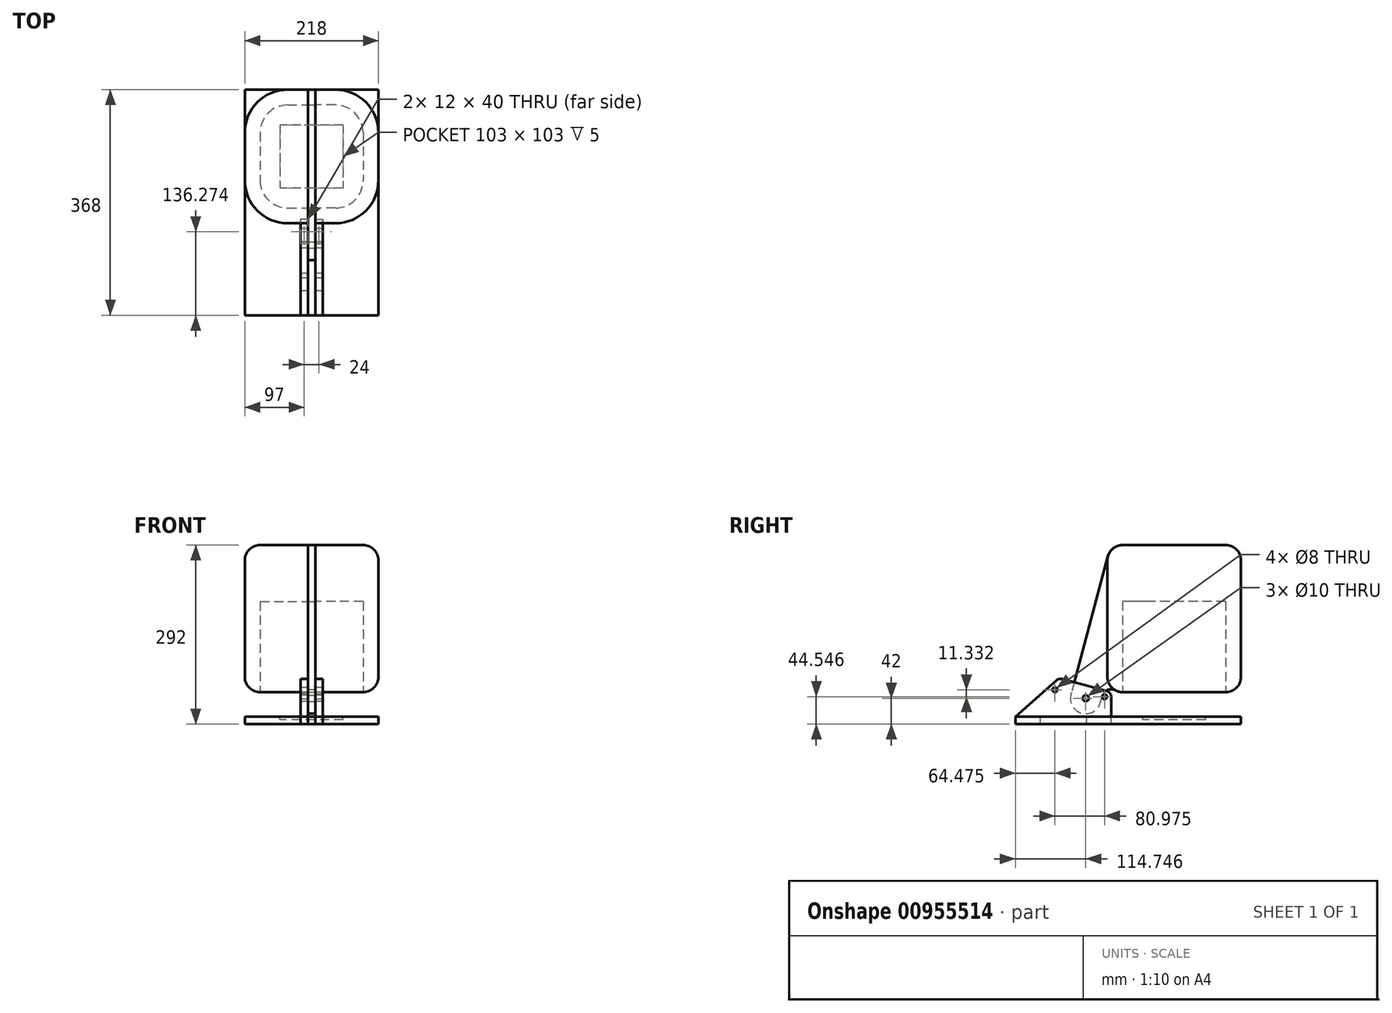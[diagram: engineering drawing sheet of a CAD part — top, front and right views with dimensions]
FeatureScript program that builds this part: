
annotation { "Feature Type Name" : "Feature", "Feature Type Description" : "" }
export const myFeature = defineFeature(function(context is Context, id is Id, definition is map)
    precondition{}
    {
        {
            assignVariable(context, id + "F0", {"name" : "mdf", "anyValue" : 12});
        }
        {
            var Q0;
            Q0=qCreatedBy(makeId("Right.planeOp"),FACE);
            var sketch = newSketch(context, id + "F1", { "sketchPlane" : qUnion([Q0])});
            skLineSegment(sketch, "E0.bottom", {"start": v(0, 0) * mm, "end": v(-35, 0) * mm});
            skLineSegment(sketch, "E0.top", {"start": v(0, 240) * mm, "end": v(-218, 240) * mm});
            skLineSegment(sketch, "E0.left", {"start": v(0, 0) * mm, "end": v(0, 240) * mm});
            skLineSegment(sketch, "E0.right", {"start": v(-218, 0) * mm, "end": v(-218, 240) * mm});
            skLineSegment(sketch, "E1.top", {"start": v(-183, 145) * mm, "end": v(-35, 145) * mm});
            skLineSegment(sketch, "E1.left", {"start": v(-183, 0) * mm, "end": v(-183, 145) * mm});
            skLineSegment(sketch, "E1.right", {"start": v(-35, 0) * mm, "end": v(-35, 145) * mm});
            skLineSegment(sketch, "E2.trimOffspring", {"start": v(-183, 0) * mm, "end": v(-218, 0) * mm});
            skLineSegment(sketch, "E3", {"start": v(-35, 0) * mm, "end": v(-183, 0) * mm});
            skSolve(sketch);
        }
        {
            var Q0;
            Q0 = qSketchRegion(id + "F1", true);
            extrude(context, id + "F2", {"entities" : qUnion([Q0]), "depth" : 103 * mm, "offsetDistance" : 25 * mm});
        }
        {
            var Q0;
            Q0=makeQuery(id+"F2.opExtrude","CAP_EDGE",EDGE,{"disambiguationData":[OSD([sQuery(id+"F1.wireOp",EDGE,"E0.left")])],"isStart":false});
            var Q1;
            Q1=makeQuery(id+"F2.opExtrude","CAP_EDGE",EDGE,{"disambiguationData":[OSD([sQuery(id+"F1.wireOp",EDGE,"E0.right")])],"isStart":false});
            fillet(context, id + "F3", {"entities" : qUnion([Q0, Q1]), "radius" : 70 * mm, "tangentPropagation" : true, "allowEdgeOverflow" : false});
        }
        {
            var Q0;
            Q0=makeQuery(id+"F2.opExtrude","SWEPT_EDGE",EDGE,{"disambiguationData":[OSD([sQuery(id+"F1.wireOp",EDGE,"E0.top"),sQuery(id+"F1.wireOp",EDGE,"E0.left")])]});
            var Q1;
            Q1=makeQuery(id+"F2.opExtrude","SWEPT_EDGE",EDGE,{"disambiguationData":[OSD([sQuery(id+"F1.wireOp",EDGE,"E0.bottom"),sQuery(id+"F1.wireOp",EDGE,"E0.left")])]});
            fillet(context, id + "F4", {"entities" : qUnion([Q0, Q1]), "radius" : 25 * mm, "tangentPropagation" : true, "allowEdgeOverflow" : false});
        }
        {
            var Q0;
            Q0=makeQuery(id+"F2.opExtrude","SWEPT_FACE",FACE,{"disambiguationData":[OSD([sQuery(id+"F1.wireOp",EDGE,"E0.bottom"),sQuery(id+"F1.wireOp",EDGE,"E2.trimOffspring"),sQuery(id+"F1.wireOp",EDGE,"E3")])]});
            var sketch = newSketch(context, id + "F5", { "sketchPlane" : qUnion([Q0])});
            skLineSegment(sketch, "E4.0", {"start": v(0, 25) * mm, "end": v(0, 193) * mm});
            skLineSegment(sketch, "E4.1", {"start": v(0, 25) * mm, "end": v(33, 25) * mm});
            skArc(sketch, "E4.2", {"start": v(33, 25) * mm, "mid": v(64.82, 38.18) * mm, "end": v(78, 70) * mm});
            skLineSegment(sketch, "E4.3", {"start": v(78, 70) * mm, "end": v(78, 148) * mm});
            skArc(sketch, "E4.4", {"start": v(78, 148) * mm, "mid": v(64.82, 179.82) * mm, "end": v(33, 193) * mm});
            skLineSegment(sketch, "E4.5", {"start": v(33, 193) * mm, "end": v(0, 193) * mm});
            skSolve(sketch);
        }
        {
            var Q0;
            Q0 = qSketchRegion(id + "F5", true);
            extrude(context, id + "F6", {"entities" : qUnion([Q0]), "operationType" : NewBodyOperationType.REMOVE, "oppositeDirection" : true, "depth" : 148 * mm, "offsetDistance" : 25 * mm});
        }
        {
            var Q0;
            Q0=makeQuery(id+"F2.opExtrude","SWEPT_BODY",BODY,{"disambiguationData":[OSD([sQuery(id+"F1.wireOp",EDGE,"E0.bottom"),sQuery(id+"F1.wireOp",EDGE,"E0.top"),sQuery(id+"F1.wireOp",EDGE,"E0.left"),sQuery(id+"F1.wireOp",EDGE,"E0.right"),sQuery(id+"F1.wireOp",EDGE,"E2.trimOffspring"),sQuery(id+"F1.wireOp",EDGE,"E3")])]});
            transform(context, id + "F7", {"entities" : qUnion([Q0]), "transformType" : TransformType.TRANSLATION_3D, "dx" : (getVariable(context, 'mdf') / 2) * mm, "dy" : 0 * mm, "dz" : 0 * mm, "makeCopy" : false});
        }
        {
            var Q0;
            Q0=makeQuery(id+"F2.opExtrude","SWEPT_BODY",BODY,{"disambiguationData":[OSD([sQuery(id+"F1.wireOp",EDGE,"E0.bottom"),sQuery(id+"F1.wireOp",EDGE,"E0.top"),sQuery(id+"F1.wireOp",EDGE,"E0.left"),sQuery(id+"F1.wireOp",EDGE,"E0.right"),sQuery(id+"F1.wireOp",EDGE,"E2.trimOffspring"),sQuery(id+"F1.wireOp",EDGE,"E3")])]});
            var Q1;
            Q1=qCreatedBy(makeId("Right.planeOp"),FACE);
            mirror(context, id + "F8", {"entities" : qUnion([Q0]), "mirrorPlane" : qUnion([Q1])});
        }
        {
            var Q0;
            Q0=makeQuery(id+"F2.opExtrude","CAP_FACE",FACE,{"disambiguationData":[OSD([sQuery(id+"F1.wireOp",EDGE,"E0.bottom"),sQuery(id+"F1.wireOp",EDGE,"E0.top"),sQuery(id+"F1.wireOp",EDGE,"E0.left"),sQuery(id+"F1.wireOp",EDGE,"E0.right"),sQuery(id+"F1.wireOp",EDGE,"E2.trimOffspring"),sQuery(id+"F1.wireOp",EDGE,"E3")])],"isStart":true});
            var sketch = newSketch(context, id + "F9", { "sketchPlane" : qUnion([Q0])});
            skLineSegment(sketch, "E5.0", {"start": v(25, 240) * mm, "end": v(193, 240) * mm});
            skArc(sketch, "E5.1", {"start": v(25, 240) * mm, "mid": v(7.32, 232.68) * mm, "end": v(0, 215) * mm});
            skLineSegment(sketch, "E5.2", {"start": v(0, 25) * mm, "end": v(0, 215) * mm});
            skArc(sketch, "E5.3", {"start": v(0, 25) * mm, "mid": v(7.32, 7.32) * mm, "end": v(25, 0) * mm});
            skLineSegment(sketch, "E5.4", {"start": v(25, 148) * mm, "end": v(25, 0) * mm});
            skLineSegment(sketch, "E5.5", {"start": v(25, 148) * mm, "end": v(193, 148) * mm});
            skLineSegment(sketch, "E5.6", {"start": v(193, 148) * mm, "end": v(193, 0) * mm});
            skArc(sketch, "E5.7", {"start": v(193, 0) * mm, "mid": v(210.68, 7.32) * mm, "end": v(218, 25) * mm});
            skLineSegment(sketch, "E5.8", {"start": v(218, 25) * mm, "end": v(218, 215) * mm});
            skArc(sketch, "E5.9", {"start": v(218, 215) * mm, "mid": v(210.68, 232.68) * mm, "end": v(193, 240) * mm});
            skLineSegment(sketch, "E6", {"start": v(217.15, 221.47) * mm, "end": v(277.4, -3.53) * mm});
            skLineSegment(sketch, "E7", {"start": v(229.1, -16.47) * mm, "end": v(218, 25) * mm});
            skArc(sketch, "E8.filletArc", {"start": v(229.1, -16.47) * mm, "mid": v(259.72, -34.15) * mm, "end": v(277.4, -3.53) * mm});
            skLineSegment(sketch, "E9.bottom", {"start": v(0, -40) * mm, "end": v(368, -40) * mm});
            skLineSegment(sketch, "E9.top", {"start": v(0, -52) * mm, "end": v(368, -52) * mm});
            skLineSegment(sketch, "E9.left", {"start": v(0, -40) * mm, "end": v(0, -52) * mm});
            skLineSegment(sketch, "E9.right", {"start": v(368, -40) * mm, "end": v(368, -52) * mm});
            skCircle(sketch, "E10", {"center": v(253.25, -10) * mm, "radius": 5 * mm});
            skLineSegment(sketch, "E11", {"start": v(211.73, -52) * mm, "end": v(211.73, 0) * mm});
            skLineSegment(sketch, "E12", {"start": v(251.73, -52) * mm, "end": v(251.73, -40) * mm});
            skLineSegment(sketch, "E13", {"start": v(251.73, -40) * mm, "end": v(328, -40) * mm});
            skLineSegment(sketch, "E14", {"start": v(328, -40) * mm, "end": v(328, -52) * mm});
            skLineSegment(sketch, "E15", {"start": v(297.18, 22.88) * mm, "end": v(368, -40) * mm});
            skLineSegment(sketch, "E16", {"start": v(211.73, 0) * mm, "end": v(297.18, 22.88) * mm});
            skCircle(sketch, "E17", {"center": v(303.53, 3.88) * mm, "radius": 4 * mm});
            skCircle(sketch, "E18", {"center": v(222.55, -7.45) * mm, "radius": 4 * mm});
            skSolve(sketch);
        }
        {
            var Q0;
            Q0=makeQuery(id+"F9.imprint","IMPRINT",FACE,{"disambiguationData":[TD([[makeQuery(id+"F9.imprint","IMPRINT",EDGE,{"derivedFrom":sQuery(id+"F9.wireOp",EDGE,"E5.0")}),-1.0]])]});
            var Q1;
            {var subQ1=sQuery(id+"F9.wireOp",EDGE,"E5.8");var subQ3=sQuery(id+"F9.wireOp",EDGE,"E6");var subQ4=makeQuery(id+"F9.imprint","INTERSECT",VERTEX,{"derivedFrom":[subQ1,subQ3]});Q1=makeQuery(id+"F9.imprint","IMPRINT",FACE,{"disambiguationData":[TD([[makeQuery(id+"F9.imprint","IMPRINT",EDGE,{"disambiguationData":[TD([[subQ4,-1.0]])],"derivedFrom":subQ3}),-1.0]])]});}
            var Q2;
            {var subQ0=sQuery(id+"F9.wireOp",EDGE,"E8.filletArc");Q2=makeQuery(id+"F9.imprint","IMPRINT",FACE,{"disambiguationData":[TD([[makeQuery(id+"F9.imprint","IMPRINT",EDGE,{"derivedFrom":subQ0}),1.0]])]});}
            extrude(context, id + "F10", {"entities" : qUnion([Q0, Q1, Q2]), "depth" : (getVariable(context, 'mdf')) * mm, "offsetDistance" : 25 * mm});
        }
        {
            var Q0;
            {var subQ0=sQuery(id+"F9.wireOp",EDGE,"E8.filletArc");Q0=makeQuery(id+"F9.imprint","IMPRINT",FACE,{"disambiguationData":[TD([[makeQuery(id+"F9.imprint","IMPRINT",EDGE,{"derivedFrom":subQ0}),1.0]])]});}
            var Q1;
            {var subQ0=sQuery(id+"F9.wireOp",EDGE,"E8.filletArc");Q1=makeQuery(id+"F9.imprint","IMPRINT",FACE,{"disambiguationData":[TD([[makeQuery(id+"F9.imprint","IMPRINT",EDGE,{"derivedFrom":subQ0}),-1.0]])]});}
            var Q2;
            {var subQ0=sQuery(id+"F9.wireOp",EDGE,"E9.right");Q2=makeQuery(id+"F9.imprint","IMPRINT",FACE,{"disambiguationData":[TD([[makeQuery(id+"F9.imprint","IMPRINT",EDGE,{"derivedFrom":subQ0}),-1.0]])]});}
            var Q3;
            {var subQ0=sQuery(id+"F9.wireOp",EDGE,"E12");Q3=makeQuery(id+"F9.imprint","IMPRINT",FACE,{"disambiguationData":[TD([[makeQuery(id+"F9.imprint","IMPRINT",EDGE,{"derivedFrom":subQ0}),1.0]])]});}
            extrude(context, id + "F11", {"entities" : qUnion([Q0, Q1, Q2, Q3]), "oppositeDirection" : true, "depth" : (getVariable(context, 'mdf')) * mm, "offsetDistance" : 25 * mm});
        }
        {
            var Q0;
            Q0=makeQuery(id+"F11.opExtrude","SWEPT_BODY",BODY,{"disambiguationData":[OSD([sQuery(id+"F9.wireOp",EDGE,"E9.top"),sQuery(id+"F9.wireOp",EDGE,"E9.right"),sQuery(id+"F9.wireOp",EDGE,"E10"),sQuery(id+"F9.wireOp",EDGE,"E11"),sQuery(id+"F9.wireOp",EDGE,"E12"),sQuery(id+"F9.wireOp",EDGE,"E13"),sQuery(id+"F9.wireOp",EDGE,"E14"),sQuery(id+"F9.wireOp",EDGE,"E15"),sQuery(id+"F9.wireOp",EDGE,"E16")])]});
            transform(context, id + "F12", {"entities" : qUnion([Q0]), "transformType" : TransformType.TRANSLATION_3D, "dx" : (-(getVariable(context, 'mdf')) * 2) * mm, "dy" : 0 * mm, "dz" : 0 * mm, "makeCopy" : true});
        }
        {
            var Q0;
            {var subQ0=sQuery(id+"F9.wireOp",EDGE,"E9.left");Q0=makeQuery(id+"F9.imprint","IMPRINT",FACE,{"disambiguationData":[TD([[makeQuery(id+"F9.imprint","IMPRINT",EDGE,{"derivedFrom":subQ0}),1.0]])]});}
            var Q1;
            {var subQ0=sQuery(id+"F9.wireOp",EDGE,"E12");Q1=makeQuery(id+"F9.imprint","IMPRINT",FACE,{"disambiguationData":[TD([[makeQuery(id+"F9.imprint","IMPRINT",EDGE,{"derivedFrom":subQ0}),1.0]])]});}
            var Q2;
            {var subQ0=sQuery(id+"F9.wireOp",EDGE,"E12");Q2=makeQuery(id+"F9.imprint","IMPRINT",FACE,{"disambiguationData":[TD([[makeQuery(id+"F9.imprint","IMPRINT",EDGE,{"derivedFrom":subQ0}),-1.0]])]});}
            var Q3;
            {var subQ0=sQuery(id+"F9.wireOp",EDGE,"E9.right");Q3=makeQuery(id+"F9.imprint","IMPRINT",FACE,{"disambiguationData":[TD([[makeQuery(id+"F9.imprint","IMPRINT",EDGE,{"derivedFrom":subQ0}),-1.0]])]});}
            var Q4;
            Q4=makeQuery(id+"F8.opPattern","COPY",FACE,{"derivedFrom":makeQuery(id+"F2.opExtrude","CAP_FACE",FACE,{"disambiguationData":[OSD([sQuery(id+"F1.wireOp",EDGE,"E0.bottom"),sQuery(id+"F1.wireOp",EDGE,"E0.top"),sQuery(id+"F1.wireOp",EDGE,"E0.left"),sQuery(id+"F1.wireOp",EDGE,"E0.right"),sQuery(id+"F1.wireOp",EDGE,"E2.trimOffspring"),sQuery(id+"F1.wireOp",EDGE,"E3")])],"isStart":false}),"instanceName":"1"});
            var Q5;
            Q5=makeQuery(id+"F2.opExtrude","CAP_FACE",FACE,{"disambiguationData":[OSD([sQuery(id+"F1.wireOp",EDGE,"E0.bottom"),sQuery(id+"F1.wireOp",EDGE,"E0.top"),sQuery(id+"F1.wireOp",EDGE,"E0.left"),sQuery(id+"F1.wireOp",EDGE,"E0.right"),sQuery(id+"F1.wireOp",EDGE,"E2.trimOffspring"),sQuery(id+"F1.wireOp",EDGE,"E3")])],"isStart":false});
            extrude(context, id + "F13", {"entities" : qUnion([Q0, Q1, Q2, Q3]), "endBound" : BoundingType.UP_TO_SURFACE, "depth" : 232 * mm, "endBoundEntityFace" : qUnion([Q4]), "offsetDistance" : 25 * mm, "hasSecondDirection" : true, "secondDirectionBound" : BoundingType.UP_TO_SURFACE, "secondDirectionOppositeDirection" : true, "secondDirectionDepth" : 25 * mm, "secondDirectionBoundEntityFace" : qUnion([Q5])});
        }
        {
            var Q0;
            Q0=makeQuery(id+"F12.opPattern","COPY",EDGE,{"derivedFrom":makeQuery(id+"F11.opExtrude","SWEPT_EDGE",EDGE,{"disambiguationData":[OSD([sQuery(id+"F9.wireOp",EDGE,"E15"),sQuery(id+"F9.wireOp",EDGE,"E16")])]}),"instanceName":"1"});
            var Q1;
            Q1=makeQuery(id+"F11.opExtrude","SWEPT_EDGE",EDGE,{"disambiguationData":[OSD([sQuery(id+"F9.wireOp",EDGE,"E15"),sQuery(id+"F9.wireOp",EDGE,"E16")])]});
            var Q2;
            Q2=makeQuery(id+"F12.opPattern","COPY",EDGE,{"derivedFrom":makeQuery(id+"F11.opExtrude","SWEPT_EDGE",EDGE,{"disambiguationData":[OSD([sQuery(id+"F9.wireOp",EDGE,"E11"),sQuery(id+"F9.wireOp",EDGE,"E16")])]}),"instanceName":"1"});
            var Q3;
            Q3=makeQuery(id+"F11.opExtrude","SWEPT_EDGE",EDGE,{"disambiguationData":[OSD([sQuery(id+"F9.wireOp",EDGE,"E11"),sQuery(id+"F9.wireOp",EDGE,"E16")])]});
            fillet(context, id + "F14", {"entities" : qUnion([Q0, Q1, Q2, Q3]), "radius" : 10 * mm, "tangentPropagation" : true, "allowEdgeOverflow" : false});
        }
        {
            var Q0;
            Q0=makeQuery(id+"F12.opPattern","COPY",BODY,{"derivedFrom":makeQuery(id+"F11.opExtrude","SWEPT_BODY",BODY,{"disambiguationData":[OSD([sQuery(id+"F9.wireOp",EDGE,"E9.top"),sQuery(id+"F9.wireOp",EDGE,"E9.right"),sQuery(id+"F9.wireOp",EDGE,"E10"),sQuery(id+"F9.wireOp",EDGE,"E11"),sQuery(id+"F9.wireOp",EDGE,"E12"),sQuery(id+"F9.wireOp",EDGE,"E13"),sQuery(id+"F9.wireOp",EDGE,"E14"),sQuery(id+"F9.wireOp",EDGE,"E15"),sQuery(id+"F9.wireOp",EDGE,"E16")])]}),"instanceName":"1"});
            var Q1;
            Q1=makeQuery(id+"F11.opExtrude","SWEPT_BODY",BODY,{"disambiguationData":[OSD([sQuery(id+"F9.wireOp",EDGE,"E9.top"),sQuery(id+"F9.wireOp",EDGE,"E9.right"),sQuery(id+"F9.wireOp",EDGE,"E10"),sQuery(id+"F9.wireOp",EDGE,"E11"),sQuery(id+"F9.wireOp",EDGE,"E12"),sQuery(id+"F9.wireOp",EDGE,"E13"),sQuery(id+"F9.wireOp",EDGE,"E14"),sQuery(id+"F9.wireOp",EDGE,"E15"),sQuery(id+"F9.wireOp",EDGE,"E16")])]});
            var Q2;
            Q2=makeQuery(id+"F13.opExtrude","SWEPT_BODY",BODY,{"disambiguationData":[OSD([sQuery(id+"F9.wireOp",EDGE,"E9.bottom"),sQuery(id+"F9.wireOp",EDGE,"E9.top"),sQuery(id+"F9.wireOp",EDGE,"E9.left"),sQuery(id+"F9.wireOp",EDGE,"E9.right"),sQuery(id+"F9.wireOp",EDGE,"E13")])]});
            booleanBodies(context, id + "F15", {"operationType" : BooleanOperationType.SUBTRACTION, "tools" : qUnion([Q0, Q1]), "targets" : qUnion([Q2]), "keepTools" : true});
        }
        {
            var Q0;
            Q0=makeQuery(id+"F13.opExtrude","SWEPT_FACE",FACE,{"disambiguationData":[OSD([sQuery(id+"F9.wireOp",EDGE,"E9.bottom"),sQuery(id+"F9.wireOp",EDGE,"E13")])]});
            var sketch = newSketch(context, id + "F16", { "sketchPlane" : qUnion([Q0])});
            skLineSegment(sketch, "E19.bottom", {"start": v(51.5, -57.5) * mm, "end": v(-51.5, -57.5) * mm});
            skLineSegment(sketch, "E19.top", {"start": v(51.5, -160.5) * mm, "end": v(-51.5, -160.5) * mm});
            skLineSegment(sketch, "E19.left", {"start": v(51.5, -57.5) * mm, "end": v(51.5, -160.5) * mm});
            skLineSegment(sketch, "E19.right", {"start": v(-51.5, -57.5) * mm, "end": v(-51.5, -160.5) * mm});
            skLineSegment(sketch, "E20", {"start": v(0, 0) * mm, "end": v(0, -57.5) * mm, "construction": true});
            skLineSegment(sketch, "E21", {"start": v(51.5, -109) * mm, "end": v(84, -109) * mm, "construction": true});
            skSolve(sketch);
        }
        {
            var Q0;
            Q0 = qSketchRegion(id + "F16", true);
            extrude(context, id + "F17", {"entities" : qUnion([Q0]), "operationType" : NewBodyOperationType.REMOVE, "oppositeDirection" : true, "depth" : 5 * mm, "offsetDistance" : 25 * mm});
        }
        {
            var Q0;
            Q0=makeQuery(id+"F10.opExtrude","SWEPT_EDGE",EDGE,{"disambiguationData":[OSD([sQuery(id+"F9.wireOp",EDGE,"E5.7"),sQuery(id+"F9.wireOp",EDGE,"E5.8"),sQuery(id+"F9.wireOp",EDGE,"E7")])]});
            var Q1;
            Q1=makeQuery(id+"F10.opExtrude","SWEPT_EDGE",EDGE,{"disambiguationData":[OSD([sQuery(id+"F9.wireOp",EDGE,"E5.8"),sQuery(id+"F9.wireOp",EDGE,"E6")])]});
            fillet(context, id + "F18", {"entities" : qUnion([Q0, Q1]), "radius" : 15 * mm, "tangentPropagation" : true, "allowEdgeOverflow" : false});
        }
    });
